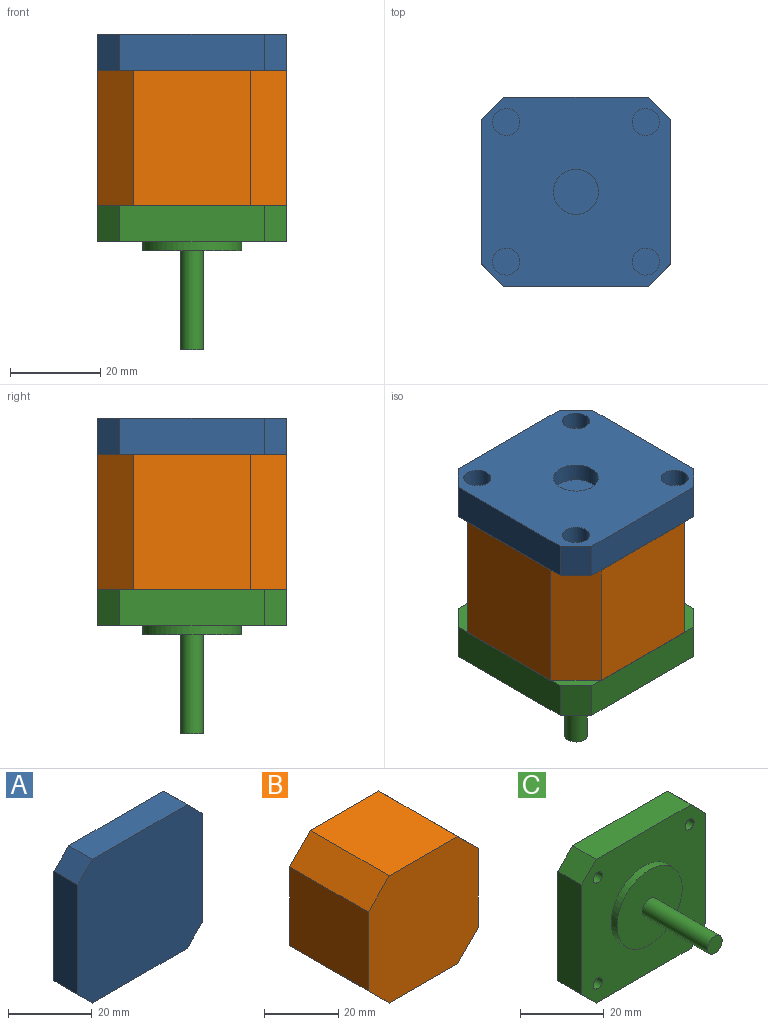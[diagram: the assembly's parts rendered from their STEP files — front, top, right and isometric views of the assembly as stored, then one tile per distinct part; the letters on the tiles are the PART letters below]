
ASSEMBLY  parts=3 mates=2
PART A: 20 faces, bbox 42x8x42 mm
  f0: plane 42x42mm, normal (0,1,0), area 1522.4mm2, adj f1,f2,f3,f4,f6,f7,f8,f9
  f1: plane 32x8mm, normal (0,0,-1), area 256mm2, adj f0,f5,f7,f9
  f2: plane 32x8mm, normal (-1,0,0), area 256mm2, adj f0,f5,f8,f9
  f3: plane 32x8mm, normal (0,0,1), area 256mm2, adj f0,f5,f6,f8
  f4: plane 32x8mm, normal (1,0,0), area 256mm2, adj f0,f5,f6,f7
  f5: plane 42x42mm, normal (0,-1,0), area 1714mm2, adj f1,f2,f3,f4,f6,f7,f8,f9
  f6: plane 8x5mm, normal (0.71,0,0.71), area 56.6mm2, adj f0,f3,f4,f5
  f7: plane 8x5mm, normal (0.71,0,-0.71), area 56.6mm2, adj f0,f1,f4,f5
  f8: plane 8x5mm, normal (-0.71,0,0.71), area 56.6mm2, adj f0,f2,f3,f5
  f9: plane 8x5mm, normal (-0.71,0,-0.71), area 56.6mm2, adj f0,f1,f2,f5
  f10: cylinder r=5mm len=10mm, axis (0,1,0), area 125.7mm2, adj f0,f11
  f11: plane 10x10mm, normal (0,1,0), area 78.5mm2, adj f10
  f12: cylinder r=3mm len=6mm, axis (0,1,0), area 75.4mm2, adj f0,f13
  f13: plane 6x6mm, normal (0,1,0), area 28.3mm2, adj f12
  f14: cylinder r=3mm len=6mm, axis (0,1,0), area 75.4mm2, adj f0,f15
  f15: plane 6x6mm, normal (0,1,0), area 28.3mm2, adj f14
  f16: cylinder r=3mm len=6mm, axis (0,1,0), area 75.4mm2, adj f0,f17
  f17: plane 6x6mm, normal (0,1,0), area 28.3mm2, adj f16
  f18: cylinder r=3mm len=6mm, axis (0,1,0), area 75.4mm2, adj f0,f19
  f19: plane 6x6mm, normal (0,1,0), area 28.3mm2, adj f18
PART B: 10 faces, bbox 42x30x42 mm
  f0: plane 30x26mm, normal (0,0,-1), area 780mm2, adj f4,f5,f6,f9
  f1: plane 30x26mm, normal (-1,0,0), area 780mm2, adj f4,f5,f8,f9
  f2: plane 30x26mm, normal (0,0,1), area 780mm2, adj f4,f5,f7,f8
  f3: plane 30x26mm, normal (1,0,0), area 780mm2, adj f4,f5,f6,f7
  f4: plane 42x42mm, normal (0,1,0), area 1636mm2, adj f0,f1,f2,f3,f6,f7,f8,f9
  f5: plane 42x42mm, normal (0,-1,0), area 1636mm2, adj f0,f1,f2,f3,f6,f7,f8,f9
  f6: plane 30x8mm, normal (0.71,0,-0.71), area 339.4mm2, adj f0,f3,f4,f5
  f7: plane 30x8mm, normal (0.71,0,0.71), area 339.4mm2, adj f2,f3,f4,f5
  f8: plane 30x8mm, normal (-0.71,0,0.71), area 339.4mm2, adj f1,f2,f4,f5
  f9: plane 30x8mm, normal (-0.71,0,-0.71), area 339.4mm2, adj f0,f1,f4,f5
PART C: 18 faces, bbox 42x32x42 mm
  f0: cylinder r=11mm len=22mm, axis (0,1,0), area 138.2mm2, adj f1,f11
  f1: plane 22x22mm, normal (0,-1,0), area 360.5mm2, adj f0,f16
  f2: plane 32x8mm, normal (0,0,-1), area 256mm2, adj f10,f11,f13,f15
  f3: plane 32x8mm, normal (-1,0,0), area 256mm2, adj f10,f11,f14,f15
  f4: plane 32x8mm, normal (0,0,1), area 256mm2, adj f10,f11,f12,f14
  f5: plane 32x8mm, normal (1,0,0), area 256mm2, adj f10,f11,f12,f13
  f6: cylinder r=1.5mm len=8mm, axis (0,-1,0), area 75.4mm2, adj f10,f11
  f7: cylinder r=1.5mm len=8mm, axis (0,-1,0), area 75.4mm2, adj f10,f11
  f8: cylinder r=1.5mm len=8mm, axis (0,-1,0), area 75.4mm2, adj f10,f11
  f9: cylinder r=1.5mm len=8mm, axis (0,-1,0), area 75.4mm2, adj f10,f11
  f10: plane 42x42mm, normal (0,1,0), area 1685.7mm2, adj f2,f3,f4,f5,f6,f7,f8,f9
  f11: plane 42x42mm, normal (0,-1,0), area 1305.6mm2, adj f0,f2,f3,f4,f5,f6,f7,f8
  f12: plane 8x5mm, normal (0.71,0,0.71), area 56.6mm2, adj f4,f5,f10,f11
  f13: plane 8x5mm, normal (0.71,0,-0.71), area 56.6mm2, adj f2,f5,f10,f11
  f14: plane 8x5mm, normal (-0.71,0,0.71), area 56.6mm2, adj f3,f4,f10,f11
  f15: plane 8x5mm, normal (-0.71,0,-0.71), area 56.6mm2, adj f2,f3,f10,f11
  f16: cylinder r=2.5mm len=22mm, axis (0,1,0), area 345.6mm2, adj f1,f17
  f17: plane 5x5mm, normal (0,-1,0), area 19.6mm2, adj f16
PLACE A rot(axis=(1,0,0),90deg) t=(0,0,-46)mm
PLACE B rot(axis=(1,0,0),90deg) t=(0,0,-46)mm
PLACE C rot(axis=(1,0,0),90deg) t=(0,0,-46)mm
MATE fastened B.f4 <-> A.f10  axis (0,0,1) through (0,0,-8)mm
MATE fastened B.f5 <-> C.f0  axis (0,0,-1) through (0,0,-38)mm
